# Revit family: Faucet-Two_Handle-American_Standard-Yoke-8344012
name_source: partatom
category: Plumbing Fixtures
units: mm (PartAtom-declared; Revit-internal decimal feet)

## family parameters
Cut with Voids When Loaded = No
Host = Face
OmniClass Number = 23.45.55.17
OmniClass Title = Mixing Faucets
Part Type = Normal
Room Calculation Point = No
Round Connector Dimension = Use Diameter
Shared = Yes

## types (1)
- 8344012.002
    ADA Compliant = Yes
    Assembly Code = D2020300
    CW Connection = Yes
    CWFU = 1.5
    Cold Water Connection Diameter = 1/2"
    Default Elevation = 0"
    Description = Top Brace Wall-Mount Service Sink Faucet with 6-Inch Vacuum Breaker Spout
    Finish = Brass-American Standard-002-Polished Chrome
    HW Connection = Yes
    HWFU = 1.5
    Hot Water Connection Diameter = 1/2"
    IAPMO Compliance = These products meet or exceed the following codes and standards: ASME A112.18.1, CSA B125.1, ANSI A117.1
    Installation Type = Wall Mounted
    Length = 12 1/2"
    Manufacturer = American Standard
    Material = Brass-American Standard-002-Polished Chrome
    Model = 8344012.002
    Price = Prices may vary. Please consult Manufacturer Representative for most up-to-date price list.
    Product Documentation Link = https://americanstandard.box.com
    Product Page URL = https://www.americanstandard-us.com
    Revised Date = 02/21/2023
    URL = http://www.americanstandard-us.com
    Vent Connection = No
    WFU = 0
    Waste Connection = No
    Width = 9 3/8"

## geometry (parser evidence)
native form markers: Sweep x2
no freeform markers — native parametric forms only
